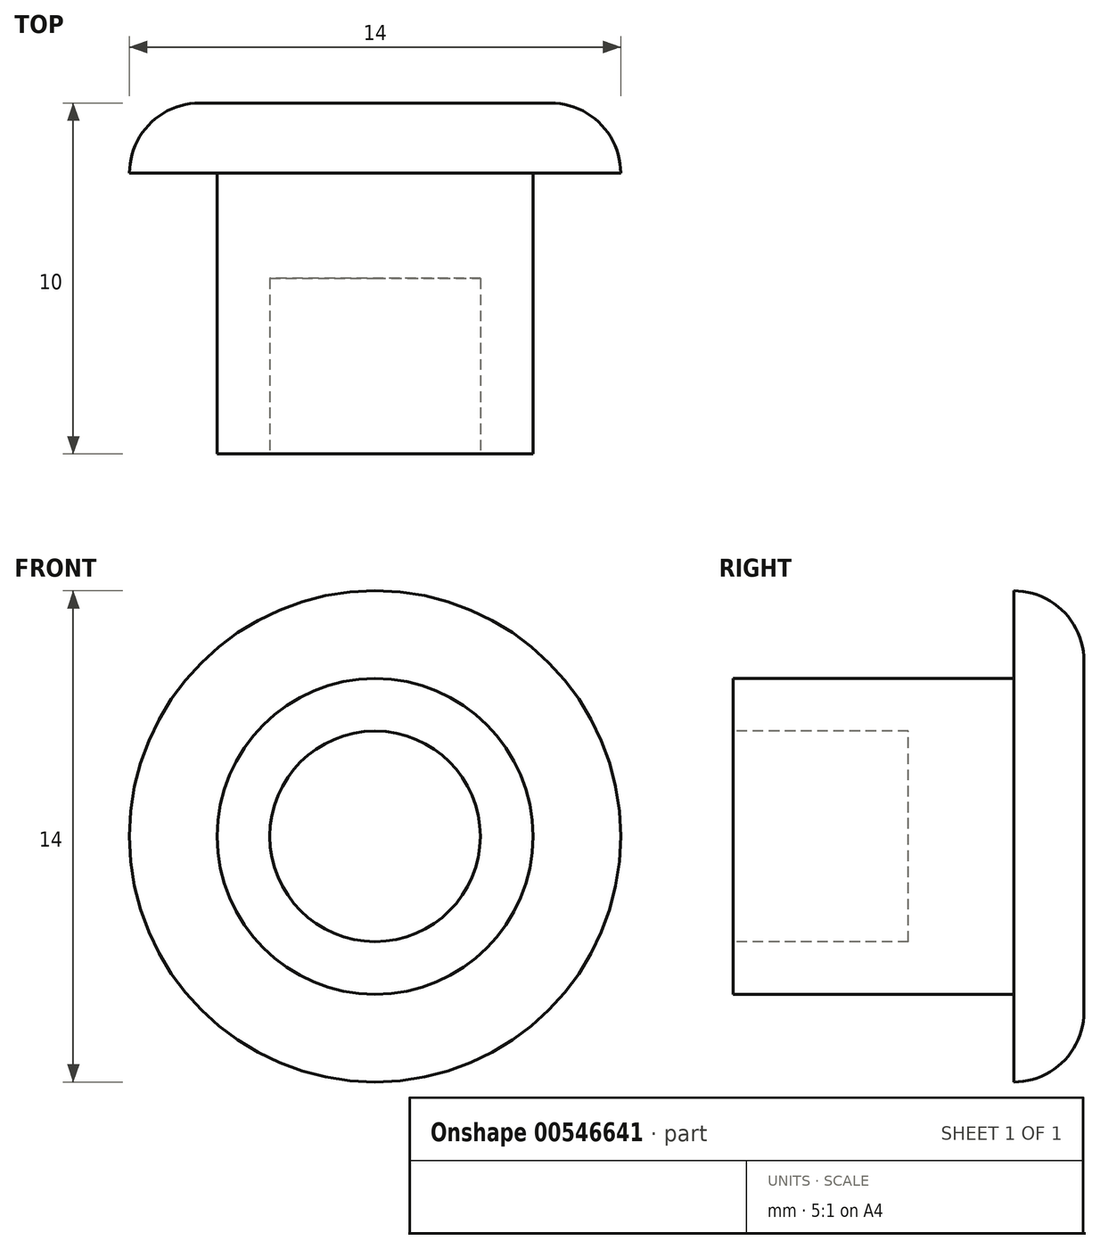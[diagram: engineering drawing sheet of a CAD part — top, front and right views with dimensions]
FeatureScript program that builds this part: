
annotation { "Feature Type Name" : "Feature", "Feature Type Description" : "" }
export const myFeature = defineFeature(function(context is Context, id is Id, definition is map)
    precondition{}
    {
        {
            var Q0;
            Q0=qCreatedBy(makeId("Front.planeOp"),FACE);
            var sketch = newSketch(context, id + "F0", { "sketchPlane" : qUnion([Q0])});
            skCircle(sketch, "E0", {"center": v(0, 0) * mm, "radius": 4.5 * mm});
            skCircle(sketch, "E1", {"center": v(0, 0) * mm, "radius": 7 * mm});
            skSolve(sketch);
        }
        {
            var Q0;
            Q0=makeQuery(id+"F0.imprint","IMPRINT",FACE,{"disambiguationData":[TD([[makeQuery(id+"F0.imprint","IMPRINT",EDGE,{"derivedFrom":sQuery(id+"F0.wireOp",EDGE,"E0")}),1.0]])]});
            extrude(context, id + "F1", {"entities" : qUnion([Q0]), "depth" : 8 * mm, "offsetDistance" : 25 * mm});
        }
        {
            var Q0;
            Q0=makeQuery(id+"F0.imprint","IMPRINT",FACE,{"disambiguationData":[TD([[makeQuery(id+"F0.imprint","IMPRINT",EDGE,{"derivedFrom":sQuery(id+"F0.wireOp",EDGE,"E0")}),-1.0]])]});
            var Q1;
            Q1=makeQuery(id+"F0.imprint","IMPRINT",FACE,{"disambiguationData":[TD([[makeQuery(id+"F0.imprint","IMPRINT",EDGE,{"derivedFrom":sQuery(id+"F0.wireOp",EDGE,"E0")}),1.0]])]});
            extrude(context, id + "F2", {"entities" : qUnion([Q0, Q1]), "operationType" : NewBodyOperationType.ADD, "oppositeDirection" : true, "depth" : 2 * mm, "offsetDistance" : 25 * mm});
        }
        {
            var Q0;
            Q0=makeQuery(id+"F2.opExtrude","CAP_EDGE",EDGE,{"disambiguationData":[OSD([sQuery(id+"F0.wireOp",EDGE,"E1")])],"isStart":false});
            fillet(context, id + "F3", {"entities" : qUnion([Q0]), "radius" : 2 * mm, "tangentPropagation" : true, "allowEdgeOverflow" : false});
        }
        {
            var Q0;
            Q0=makeQuery(id+"F1.opExtrude","CAP_FACE",FACE,{"disambiguationData":[OSD([sQuery(id+"F0.wireOp",EDGE,"E0")])],"isStart":false});
            var sketch = newSketch(context, id + "F4", { "sketchPlane" : qUnion([Q0])});
            skCircle(sketch, "E2", {"center": v(0, 0) * mm, "radius": 3 * mm});
            skSolve(sketch);
        }
        {
            var Q0;
            Q0=makeQuery(id+"F4.imprint","IMPRINT",FACE,{"disambiguationData":[TD([[makeQuery(id+"F4.imprint","IMPRINT",EDGE,{"derivedFrom":sQuery(id+"F4.wireOp",EDGE,"E2")}),1.0]])]});
            extrude(context, id + "F5", {"entities" : qUnion([Q0]), "operationType" : NewBodyOperationType.REMOVE, "oppositeDirection" : true, "depth" : 5 * mm, "offsetDistance" : 25 * mm});
        }
    });
